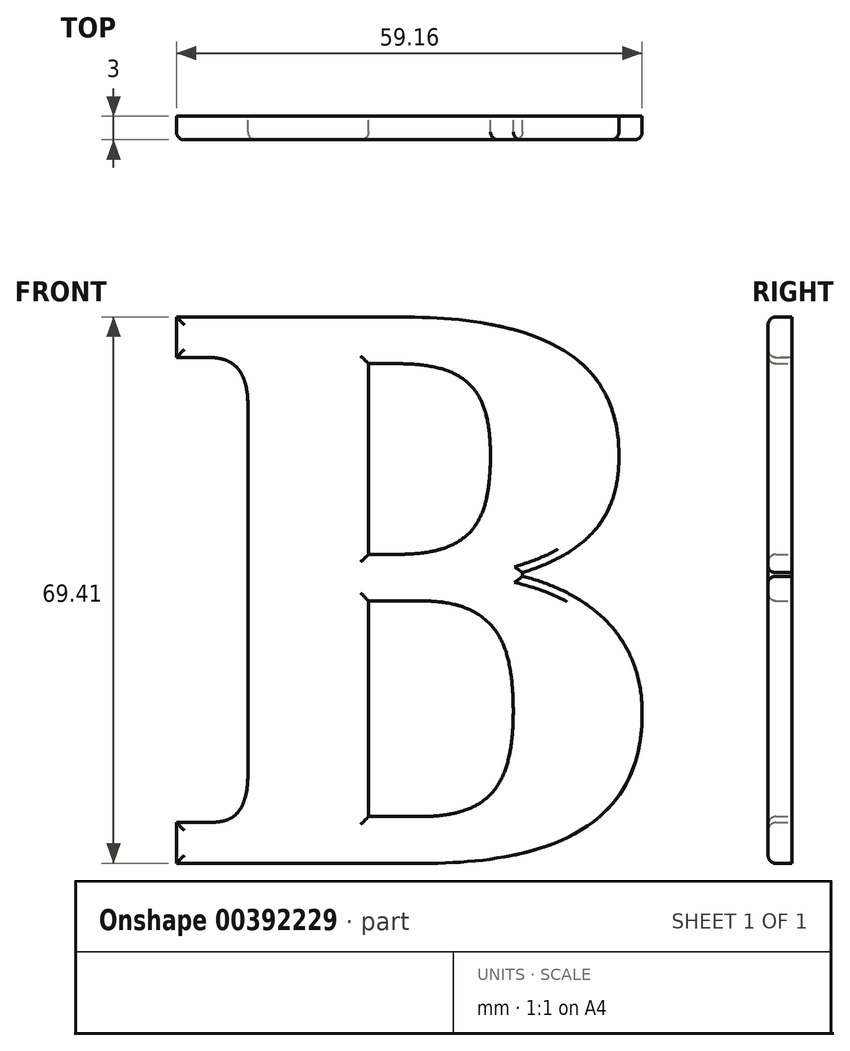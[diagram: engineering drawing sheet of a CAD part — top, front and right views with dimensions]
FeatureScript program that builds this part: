
annotation { "Feature Type Name" : "Feature", "Feature Type Description" : "" }
export const myFeature = defineFeature(function(context is Context, id is Id, definition is map)
    precondition{}
    {
        {
            var Q0;
            Q0=qCreatedBy(makeId("Front.planeOp"),FACE);
            var sketch = newSketch(context, id + "F0", { "sketchPlane" : qUnion([Q0])});
            skText(sketch, "E0", { "text": "B", "fontName": "NotoSerif-Bold.ttf"});
            const initialGuessF0  = {"E0": [0, 0, 1, 0, 0.07]};
            skSetInitialGuess(sketch, initialGuessF0);
            skSolve(sketch);
        }
        {
            var Q0;
            Q0 = qSketchRegion(id + "F0", true);
            extrude(context, id + "F1", {"entities" : qUnion([Q0]), "depth" : 3 * mm});
        }
        {
            var Q0;
            Q0=makeQuery(id+"F1.opExtrude","CAP_FACE",FACE,{"disambiguationData":[OSD([sQuery(id+"F0.wireOp",EDGE,"E0.sketch_text.stroke-0"),sQuery(id+"F0.wireOp",EDGE,"E0.sketch_text.stroke-1"),sQuery(id+"F0.wireOp",EDGE,"E0.sketch_text.stroke-2"),sQuery(id+"F0.wireOp",EDGE,"E0.sketch_text.stroke-3"),sQuery(id+"F0.wireOp",EDGE,"E0.sketch_text.stroke-4"),sQuery(id+"F0.wireOp",EDGE,"E0.sketch_text.stroke-5"),sQuery(id+"F0.wireOp",EDGE,"E0.sketch_text.stroke-6"),sQuery(id+"F0.wireOp",EDGE,"E0.sketch_text.stroke-7"),sQuery(id+"F0.wireOp",EDGE,"E0.sketch_text.stroke-8"),sQuery(id+"F0.wireOp",EDGE,"E0.sketch_text.stroke-9"),sQuery(id+"F0.wireOp",EDGE,"E0.sketch_text.stroke-10"),sQuery(id+"F0.wireOp",EDGE,"E0.sketch_text.stroke-11"),sQuery(id+"F0.wireOp",EDGE,"E0.sketch_text.stroke-12"),sQuery(id+"F0.wireOp",EDGE,"E0.sketch_text.stroke-13"),sQuery(id+"F0.wireOp",EDGE,"E0.sketch_text.stroke-14"),sQuery(id+"F0.wireOp",EDGE,"E0.sketch_text.stroke-15"),sQuery(id+"F0.wireOp",EDGE,"E0.sketch_text.stroke-16"),sQuery(id+"F0.wireOp",EDGE,"E0.sketch_text.stroke-17"),sQuery(id+"F0.wireOp",EDGE,"E0.sketch_text.stroke-18"),sQuery(id+"F0.wireOp",EDGE,"E0.sketch_text.stroke-19"),sQuery(id+"F0.wireOp",EDGE,"E0.sketch_text.stroke-20"),sQuery(id+"F0.wireOp",EDGE,"E0.sketch_text.stroke-21"),sQuery(id+"F0.wireOp",EDGE,"E0.sketch_text.stroke-22"),sQuery(id+"F0.wireOp",EDGE,"E0.sketch_text.stroke-23"),sQuery(id+"F0.wireOp",EDGE,"E0.sketch_text.stroke-24"),sQuery(id+"F0.wireOp",EDGE,"E0.sketch_text.stroke-25"),sQuery(id+"F0.wireOp",EDGE,"E0.sketch_text.stroke-26"),sQuery(id+"F0.wireOp",EDGE,"E0.sketch_text.stroke-27"),sQuery(id+"F0.wireOp",EDGE,"E0.sketch_text.stroke-28"),sQuery(id+"F0.wireOp",EDGE,"E0.sketch_text.stroke-29"),sQuery(id+"F0.wireOp",EDGE,"E0.sketch_text.stroke-30"),sQuery(id+"F0.wireOp",EDGE,"E0.sketch_text.stroke-31"),sQuery(id+"F0.wireOp",EDGE,"E0.sketch_text.stroke-32"),sQuery(id+"F0.wireOp",EDGE,"E0.sketch_text.stroke-33"),sQuery(id+"F0.wireOp",EDGE,"E0.sketch_text.stroke-34"),sQuery(id+"F0.wireOp",EDGE,"E0.sketch_text.stroke-35"),sQuery(id+"F0.wireOp",EDGE,"E0.sketch_text.stroke-36"),sQuery(id+"F0.wireOp",EDGE,"E0.sketch_text.stroke-37"),sQuery(id+"F0.wireOp",EDGE,"E0.sketch_text.stroke-38"),sQuery(id+"F0.wireOp",EDGE,"E0.sketch_text.stroke-39"),sQuery(id+"F0.wireOp",EDGE,"E0.sketch_text.stroke-40"),sQuery(id+"F0.wireOp",EDGE,"E0.sketch_text.stroke-41"),sQuery(id+"F0.wireOp",EDGE,"E0.sketch_text.stroke-42"),sQuery(id+"F0.wireOp",EDGE,"E0.sketch_text.stroke-43"),sQuery(id+"F0.wireOp",EDGE,"E0.sketch_text.stroke-44"),sQuery(id+"F0.wireOp",EDGE,"E0.sketch_text.stroke-45"),sQuery(id+"F0.wireOp",EDGE,"E0.sketch_text.stroke-46"),sQuery(id+"F0.wireOp",EDGE,"E0.sketch_text.stroke-47"),sQuery(id+"F0.wireOp",EDGE,"E0.sketch_text.stroke-48"),sQuery(id+"F0.wireOp",EDGE,"E0.sketch_text.stroke-49")])],"isStart":false});
            fillet(context, id + "F2", {"entities" : qUnion([Q0]), "radius" : 1 * mm, "tangentPropagation" : true, "allowEdgeOverflow" : false});
        }
    });
